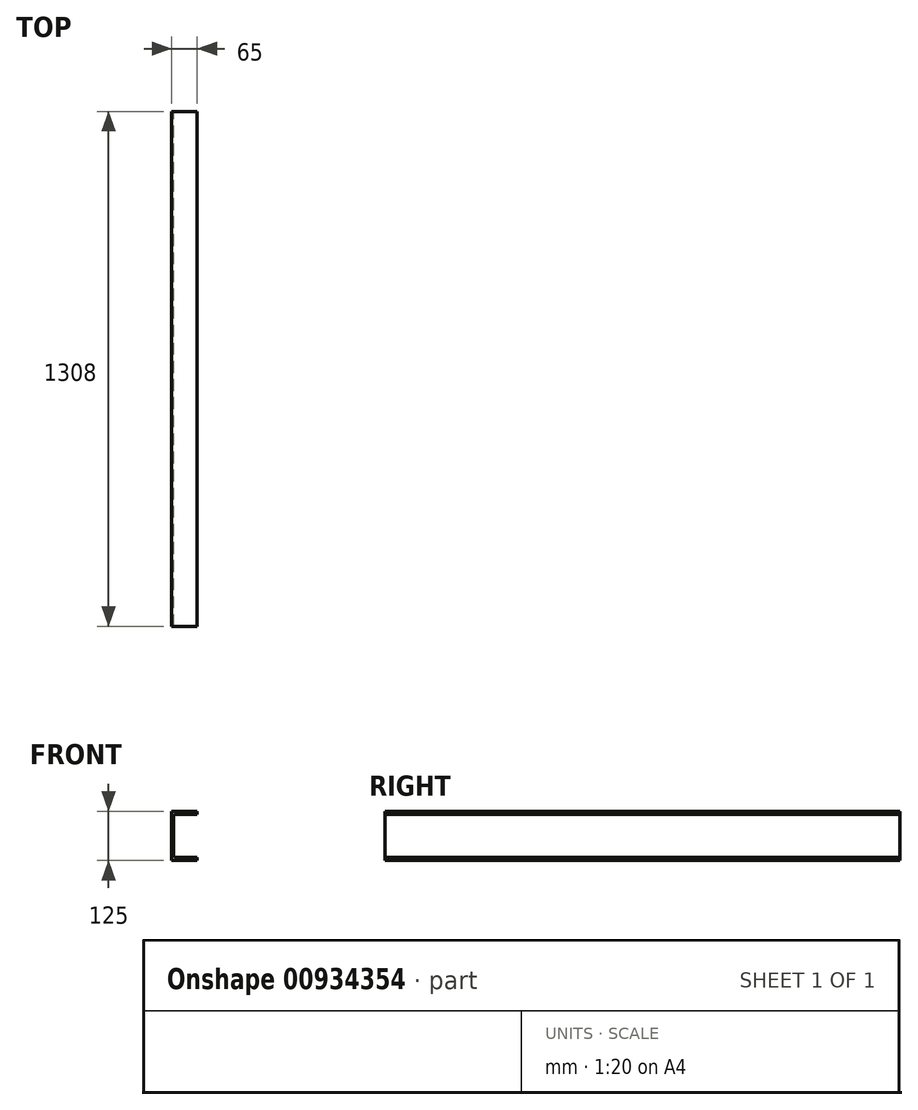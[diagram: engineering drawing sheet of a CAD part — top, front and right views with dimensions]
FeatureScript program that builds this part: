
annotation { "Feature Type Name" : "Feature", "Feature Type Description" : "" }
export const myFeature = defineFeature(function(context is Context, id is Id, definition is map)
    precondition{}
    {
        {
            var Q0;
            Q0=qCreatedBy(makeId("Front.planeOp"),FACE);
            var sketch = newSketch(context, id + "F0", { "sketchPlane" : qUnion([Q0])});
            skLineSegment(sketch, "E0", {"start": v(-25.17, -62.5) * mm, "end": v(-25.17, 62.5) * mm});
            skLineSegment(sketch, "E1", {"start": v(-25.17, 62.5) * mm, "end": v(39.83, 62.5) * mm});
            skLineSegment(sketch, "E2", {"start": v(39.83, 62.5) * mm, "end": v(39.83, 55) * mm});
            skLineSegment(sketch, "E3", {"start": v(39.83, 55) * mm, "end": v(-12.47, 55) * mm});
            skLineSegment(sketch, "E4", {"start": v(-25.17, -62.5) * mm, "end": v(39.83, -62.5) * mm});
            skLineSegment(sketch, "E5", {"start": v(39.83, -62.5) * mm, "end": v(39.83, -55) * mm});
            skLineSegment(sketch, "E6", {"start": v(39.83, -55) * mm, "end": v(-12.47, -55) * mm});
            skLineSegment(sketch, "E7", {"start": v(-20.47, -47) * mm, "end": v(-20.47, 47) * mm});
            skPoint(sketch, "E8.visualSharp", {"position": v(-20.47, 55) * mm});
            skArc(sketch, "E8.filletArc", {"start": v(-12.47, 55) * mm, "mid": v(-18.12, 52.66) * mm, "end": v(-20.47, 47) * mm});
            skPoint(sketch, "E9.visualSharp", {"position": v(-20.47, -55) * mm});
            skArc(sketch, "E9.filletArc", {"start": v(-20.47, -47) * mm, "mid": v(-18.12, -52.66) * mm, "end": v(-12.47, -55) * mm});
            skSolve(sketch);
        }
        {
            var Q0;
            Q0=makeQuery(id+"F0.imprint","IMPRINT",FACE,{"disambiguationData":[TD([[makeQuery(id+"F0.imprint","IMPRINT",EDGE,{"derivedFrom":sQuery(id+"F0.wireOp",EDGE,"E0")}),-1.0]])]});
            extrude(context, id + "F1", {"entities" : qUnion([Q0]), "depth" : 1308 * mm, "offsetDistance" : 25 * mm});
        }
    });
